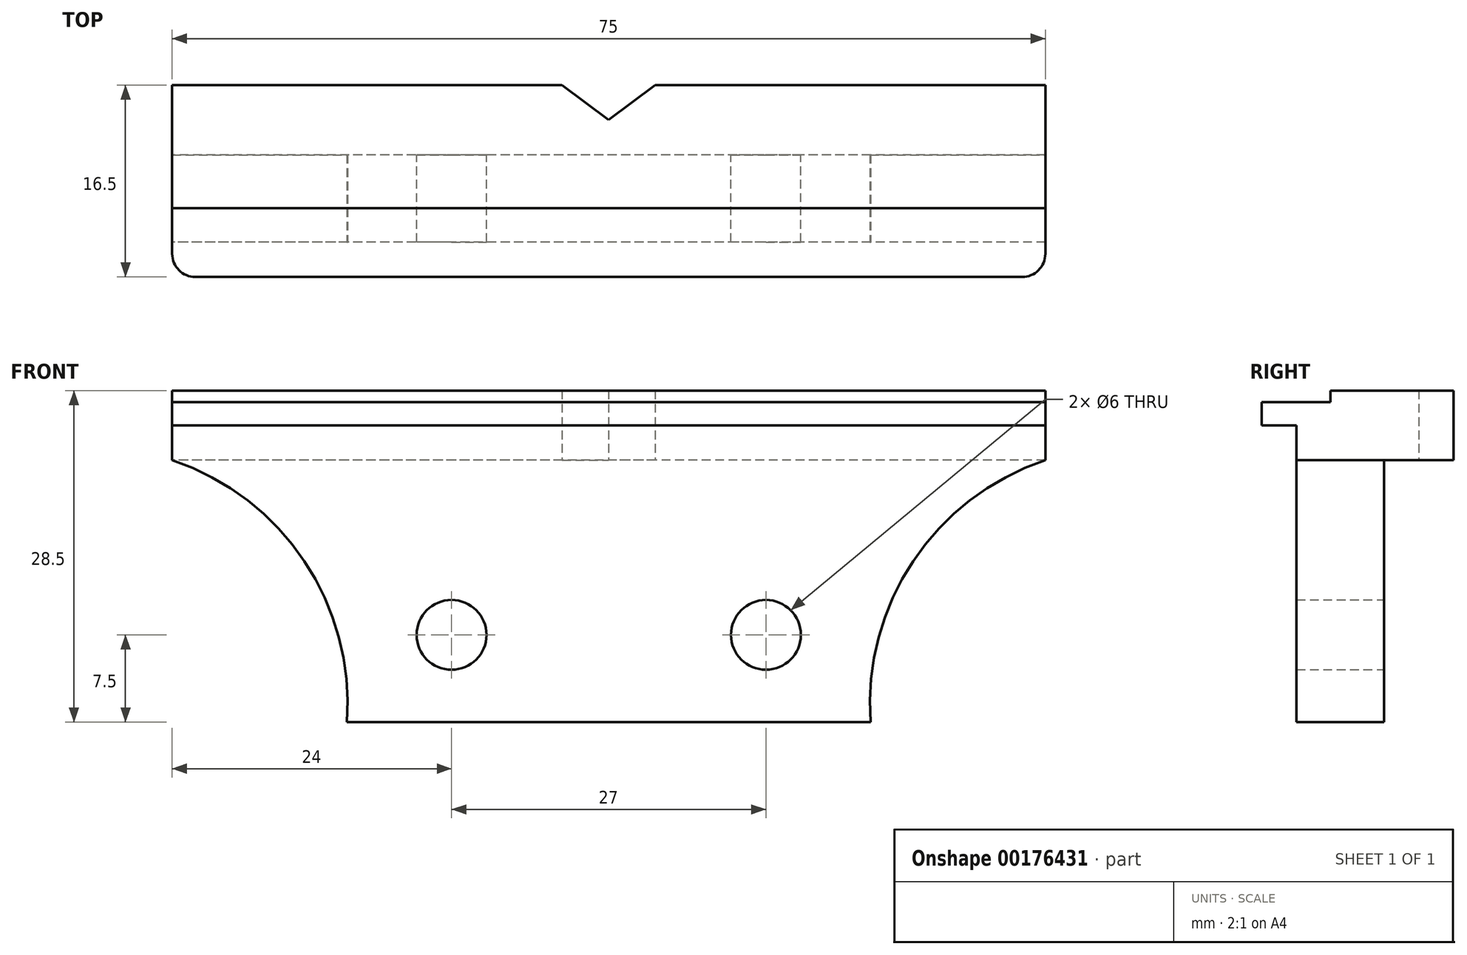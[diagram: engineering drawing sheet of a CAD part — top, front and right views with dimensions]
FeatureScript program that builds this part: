
annotation { "Feature Type Name" : "Feature", "Feature Type Description" : "" }
export const myFeature = defineFeature(function(context is Context, id is Id, definition is map)
    precondition{}
    {
        {
            var Q0;
            Q0=qCreatedBy(makeId("Right.planeOp"),FACE);
            var sketch = newSketch(context, id + "F0", { "sketchPlane" : qUnion([Q0])});
            skLineSegment(sketch, "E0", {"start": v(0, 0) * mm, "end": v(-7.5, 0) * mm});
            skLineSegment(sketch, "E1", {"start": v(-7.5, 0) * mm, "end": v(-7.5, 25.5) * mm});
            skLineSegment(sketch, "E2", {"start": v(-7.5, 25.5) * mm, "end": v(-10.5, 25.5) * mm});
            skLineSegment(sketch, "E3", {"start": v(-10.5, 25.5) * mm, "end": v(-10.5, 27.5) * mm});
            skLineSegment(sketch, "E4", {"start": v(-10.5, 27.5) * mm, "end": v(-4.57, 27.5) * mm});
            skLineSegment(sketch, "E5", {"start": v(-4.57, 27.5) * mm, "end": v(-4.57, 28.5) * mm});
            skLineSegment(sketch, "E6", {"start": v(-4.57, 28.5) * mm, "end": v(6, 28.5) * mm});
            skLineSegment(sketch, "E7", {"start": v(6, 28.5) * mm, "end": v(6, 22.5) * mm});
            skLineSegment(sketch, "E8", {"start": v(6, 22.5) * mm, "end": v(0, 22.5) * mm});
            skLineSegment(sketch, "E9", {"start": v(0, 22.5) * mm, "end": v(0, 0) * mm});
            skSolve(sketch);
        }
        {
            var Q0;
            Q0=makeQuery(id+"F0.imprint","IMPRINT",FACE,{"disambiguationData":[TD([[makeQuery(id+"F0.imprint","IMPRINT",EDGE,{"derivedFrom":sQuery(id+"F0.wireOp",EDGE,"E0")}),-1.0]])]});
            extrude(context, id + "F1", {"entities" : qUnion([Q0]), "depth" : 75 * mm});
        }
        {
            var Q0;
            Q0=qCreatedBy(makeId("Front.planeOp"),FACE);
            var sketch = newSketch(context, id + "F2", { "sketchPlane" : qUnion([Q0])});
            skArc(sketch, "E10", {"start": v(15, 0) * mm, "mid": v(11.37, 13.83) * mm, "end": v(0, 22.5) * mm});
            skLineSegment(sketch, "E11", {"start": v(0, 22.5) * mm, "end": v(-15.86, 22.5) * mm});
            skLineSegment(sketch, "E12", {"start": v(-15.86, 22.5) * mm, "end": v(-15.86, -15.02) * mm});
            skLineSegment(sketch, "E13", {"start": v(-15.86, -15.02) * mm, "end": v(18.95, -15.02) * mm});
            skLineSegment(sketch, "E14", {"start": v(18.95, -15.02) * mm, "end": v(15, 0) * mm});
            skLineSegment(sketch, "E15", {"start": v(0, 49.1) * mm, "end": v(37.5, 49.1) * mm});
            skLineSegment(sketch, "E16", {"start": v(37.5, 49.1) * mm, "end": v(37.5, -10.9) * mm});
            skLineSegment(sketch, "E17.MirrorCS", {"start": v(75, 22.5) * mm, "end": v(90.86, 22.5) * mm});
            skArc(sketch, "E18.MirrorCS", {"start": v(60, 0) * mm, "mid": v(63.63, 13.83) * mm, "end": v(75, 22.5) * mm});
            skLineSegment(sketch, "E19.MirrorCS", {"start": v(56.05, -15.02) * mm, "end": v(60, 0) * mm});
            skLineSegment(sketch, "E20.MirrorCS", {"start": v(90.86, -15.02) * mm, "end": v(56.05, -15.02) * mm});
            skLineSegment(sketch, "E21.MirrorCS", {"start": v(90.86, 22.5) * mm, "end": v(90.86, -15.02) * mm});
            skSolve(sketch);
        }
        {
            var Q0;
            Q0=qCreatedBy(makeId("Right.planeOp"),FACE);
            cPlane(context, id + "F3", {"entities" : qUnion([Q0]), "cplaneType" : CPlaneType.OFFSET, "offset" : 37.5 * mm, "width" : 150 * mm, "height" : 150 * mm});
        }
        {
            var Q0;
            Q0 = qSketchRegion(id + "F2", true);
            extrude(context, id + "F4", {"entities" : qUnion([Q0]), "operationType" : NewBodyOperationType.REMOVE, "oppositeDirection" : true, "depth" : 25 * mm, "hasSecondDirection" : true, "secondDirectionOppositeDirection" : false, "secondDirectionDepth" : 25 * mm});
        }
        {
            var Q0;
            Q0=qCreatedBy(makeId("Front.planeOp"),FACE);
            var sketch = newSketch(context, id + "F5", { "sketchPlane" : qUnion([Q0])});
            skLineSegment(sketch, "E22", {"start": v(35.85, 0) * mm, "end": v(22.35, 0) * mm});
            skCircle(sketch, "E23", {"center": v(24, 7.5) * mm, "radius": 3 * mm});
            skCircle(sketch, "E24.MirrorC", {"center": v(51, 7.5) * mm, "radius": 3 * mm});
            skSolve(sketch);
        }
        {
            var Q0;
            Q0 = qSketchRegion(id + "F5", true);
            extrude(context, id + "F6", {"entities" : qUnion([Q0]), "operationType" : NewBodyOperationType.REMOVE, "depth" : 25 * mm, "hasSecondDirection" : true, "secondDirectionOppositeDirection" : true, "secondDirectionDepth" : 25 * mm});
        }
        {
            var Q0;
            Q0=makeQuery(id+"F1.opExtrude","CAP_EDGE",EDGE,{"disambiguationData":[OSD([sQuery(id+"F0.wireOp",EDGE,"E3")])],"isStart":false});
            var Q1;
            Q1=makeQuery(id+"F1.opExtrude","CAP_EDGE",EDGE,{"disambiguationData":[OSD([sQuery(id+"F0.wireOp",EDGE,"E3")])],"isStart":true});
            fillet(context, id + "F7", {"entities" : qUnion([Q0, Q1]), "radius" : 2 * mm, "tangentPropagation" : true, "allowEdgeOverflow" : false});
        }
        {
            var Q0;
            Q0=qCreatedBy(makeId("Top.planeOp"),FACE);
            var sketch = newSketch(context, id + "F8", { "sketchPlane" : qUnion([Q0])});
            skLineSegment(sketch, "E25", {"start": v(0, 0) * mm, "end": v(37.5, 0) * mm});
            skLineSegment(sketch, "E26", {"start": v(37.5, 0) * mm, "end": v(37.5, 3) * mm});
            skLineSegment(sketch, "E27", {"start": v(33.5, 6) * mm, "end": v(37.5, 3) * mm});
            skLineSegment(sketch, "E28.MirrorCS", {"start": v(41.5, 6) * mm, "end": v(37.5, 3) * mm});
            skLineSegment(sketch, "E29", {"start": v(33.5, 6) * mm, "end": v(32.5, 11.94) * mm});
            skLineSegment(sketch, "E30", {"start": v(32.5, 11.94) * mm, "end": v(50.54, 15) * mm});
            skLineSegment(sketch, "E31", {"start": v(50.54, 15) * mm, "end": v(41.5, 6) * mm});
            skPoint(sketch, "E32.start.orphan", {"position": v(37.5, 6) * mm});
            skSolve(sketch);
        }
        {
            var Q0;
            Q0=makeQuery(id+"F8.imprint","IMPRINT",FACE,{"disambiguationData":[TD([[makeQuery(id+"F8.imprint","IMPRINT",EDGE,{"derivedFrom":sQuery(id+"F8.wireOp",EDGE,"E27")}),1.0]])]});
            extrude(context, id + "F9", {"entities" : qUnion([Q0]), "operationType" : NewBodyOperationType.REMOVE, "depth" : 50 * mm});
        }
    });
